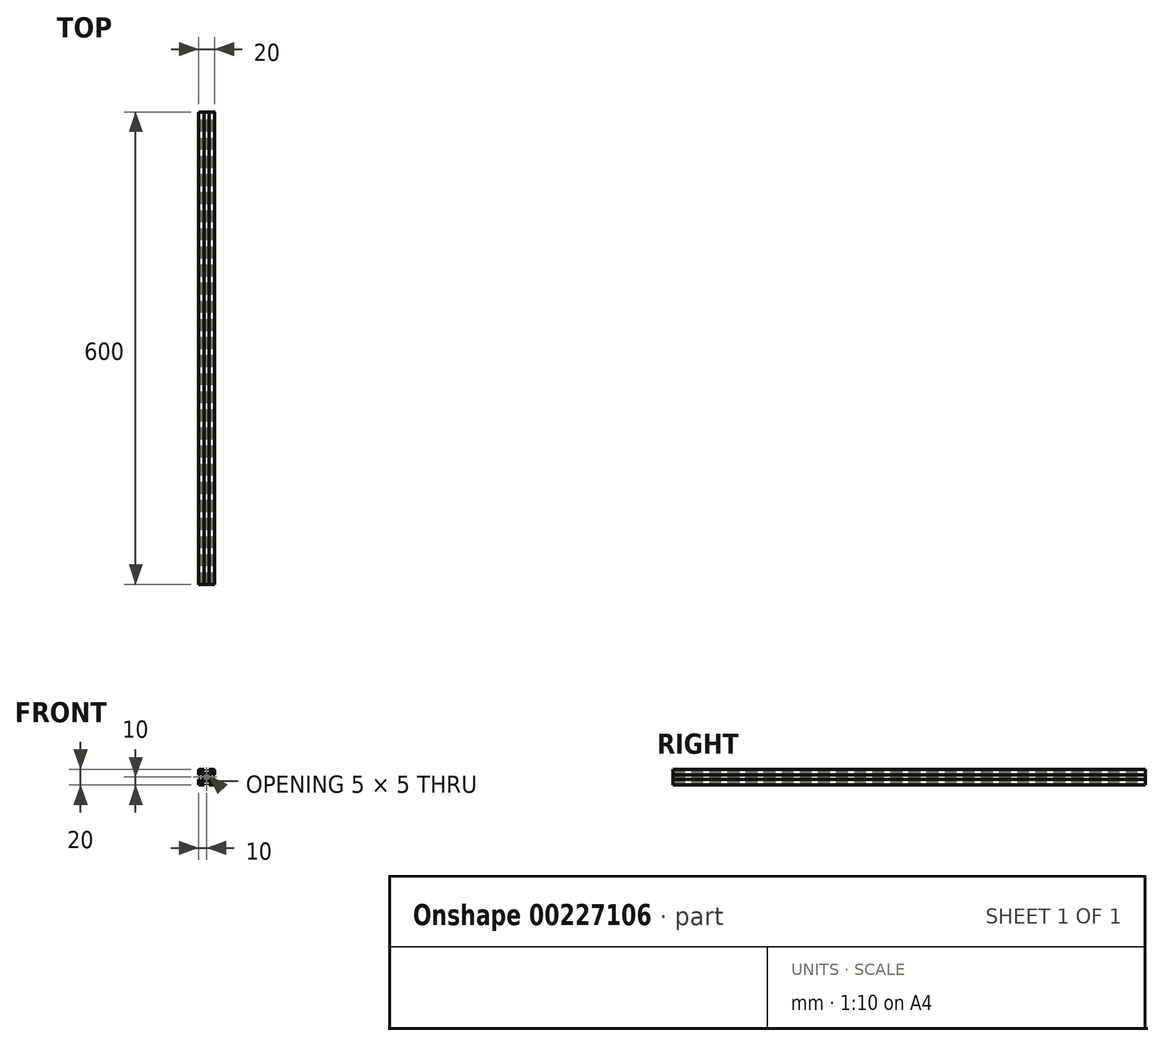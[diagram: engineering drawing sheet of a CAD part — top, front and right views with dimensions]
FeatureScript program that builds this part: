
annotation { "Feature Type Name" : "Feature", "Feature Type Description" : "" }
export const myFeature = defineFeature(function(context is Context, id is Id, definition is map)
    precondition{}
    {
        {
            var Q0;
            Q0=qCreatedBy(makeId("Front.planeOp"),FACE);
            var sketch = newSketch(context, id + "F0", { "sketchPlane" : qUnion([Q0])});
            skLineSegment(sketch, "E0.bottom", {"start": v(8.5, -10) * mm, "end": v(3, -10) * mm});
            skLineSegment(sketch, "E0.top", {"start": v(8.5, 10) * mm, "end": v(3, 10) * mm});
            skLineSegment(sketch, "E0.left", {"start": v(10, -8.5) * mm, "end": v(10, -3) * mm});
            skLineSegment(sketch, "E0.right", {"start": v(-10, -8.5) * mm, "end": v(-10, -3) * mm});
            skPoint(sketch, "E0.middle", {"position": v(0, 0) * mm});
            skLineSegment(sketch, "E1.bottom", {"start": v(6, -8.5) * mm, "end": v(3, -8.5) * mm});
            skLineSegment(sketch, "E1.top", {"start": v(6, 8.5) * mm, "end": v(3, 8.5) * mm});
            skLineSegment(sketch, "E1.left", {"start": v(8.5, -6) * mm, "end": v(8.5, -3) * mm});
            skLineSegment(sketch, "E1.right", {"start": v(-8.5, -6) * mm, "end": v(-8.5, -3) * mm});
            skLineSegment(sketch, "E2.bottom", {"start": v(3.44, -4.5) * mm, "end": v(-3.44, -4.5) * mm});
            skLineSegment(sketch, "E2.top", {"start": v(3.44, 4.5) * mm, "end": v(-3.44, 4.5) * mm});
            skLineSegment(sketch, "E2.left", {"start": v(4.5, -3.44) * mm, "end": v(4.5, 3.44) * mm});
            skLineSegment(sketch, "E2.right", {"start": v(-4.5, -3.44) * mm, "end": v(-4.5, 3.44) * mm});
            skLineSegment(sketch, "E3.bottom", {"start": v(8.5, -6) * mm, "end": v(7.06, -6) * mm});
            skLineSegment(sketch, "E3.top", {"start": v(8.5, 6) * mm, "end": v(7.06, 6) * mm});
            skLineSegment(sketch, "E4.left", {"start": v(6, -8.5) * mm, "end": v(6, -7.06) * mm});
            skLineSegment(sketch, "E4.right", {"start": v(-6, -8.5) * mm, "end": v(-6, -7.06) * mm});
            skPoint(sketch, "E5.orphan", {"position": v(-8.5, 8.5) * mm});
            skPoint(sketch, "E6.orphan", {"position": v(8.5, 8.5) * mm});
            skPoint(sketch, "E7.orphan", {"position": v(8.5, -8.5) * mm});
            skPoint(sketch, "E8.orphan", {"position": v(-8.5, -8.5) * mm});
            skLineSegment(sketch, "E9.trimOffspring", {"start": v(-6, 7.06) * mm, "end": v(-6, 8.5) * mm});
            skLineSegment(sketch, "E10.trimOffspring", {"start": v(-7.06, 6) * mm, "end": v(-8.5, 6) * mm});
            skLineSegment(sketch, "E11.trimOffspring", {"start": v(6, 7.06) * mm, "end": v(6, 8.5) * mm});
            skLineSegment(sketch, "E12.trimOffspring", {"start": v(-7.06, -6) * mm, "end": v(-8.5, -6) * mm});
            skLineSegment(sketch, "E13", {"start": v(-10, 10) * mm, "end": v(0, 0) * mm, "construction": true});
            skLineSegment(sketch, "E14", {"start": v(10, 10) * mm, "end": v(0, 0) * mm, "construction": true});
            skLineSegment(sketch, "E15", {"start": v(-6, 7.06) * mm, "end": v(-3.44, 4.5) * mm});
            skPoint(sketch, "E15.endSnap0", {"position": v(7.25, -6) * mm});
            skLineSegment(sketch, "E16", {"start": v(6, -7.06) * mm, "end": v(3.44, -4.5) * mm});
            skLineSegment(sketch, "E17", {"start": v(7.06, 6) * mm, "end": v(4.5, 3.44) * mm});
            skLineSegment(sketch, "E18", {"start": v(6, 7.06) * mm, "end": v(3.44, 4.5) * mm});
            skPoint(sketch, "E19.orphan", {"position": v(6, -6) * mm});
            skPoint(sketch, "E20.orphan", {"position": v(-4.5, -4.5) * mm});
            skPoint(sketch, "E21.orphan", {"position": v(-4.5, 4.5) * mm});
            skPoint(sketch, "E22.orphan", {"position": v(4.5, 4.5) * mm});
            skPoint(sketch, "E23.orphan", {"position": v(4.5, -4.5) * mm});
            skLineSegment(sketch, "E24.trimOffspring", {"start": v(4.5, -3.44) * mm, "end": v(7.06, -6) * mm});
            skLineSegment(sketch, "E25.trimOffspring", {"start": v(-3.44, -4.5) * mm, "end": v(-6, -7.06) * mm});
            skLineSegment(sketch, "E26.trimOffspring", {"start": v(-4.5, -3.44) * mm, "end": v(-7.06, -6) * mm});
            skLineSegment(sketch, "E27.trimOffspring", {"start": v(-4.5, 3.44) * mm, "end": v(-7.06, 6) * mm});
            skLineSegment(sketch, "E28.bottom", {"start": v(8.5, -3) * mm, "end": v(10, -3) * mm});
            skLineSegment(sketch, "E28.top", {"start": v(8.5, 3) * mm, "end": v(10, 3) * mm});
            skPoint(sketch, "E28.middle", {"position": v(10, 0) * mm});
            skLineSegment(sketch, "E29.left", {"start": v(3, 8.5) * mm, "end": v(3, 10) * mm});
            skLineSegment(sketch, "E29.right", {"start": v(-3, 8.5) * mm, "end": v(-3, 10) * mm});
            skPoint(sketch, "E29.middle", {"position": v(0, 10) * mm});
            skLineSegment(sketch, "E30.bottom", {"start": v(-8.5, 3) * mm, "end": v(-10, 3) * mm});
            skLineSegment(sketch, "E30.top", {"start": v(-8.5, -3) * mm, "end": v(-10, -3) * mm});
            skPoint(sketch, "E30.middle", {"position": v(-10, 0) * mm});
            skLineSegment(sketch, "E31.left", {"start": v(3, -8.5) * mm, "end": v(3, -10) * mm});
            skLineSegment(sketch, "E31.right", {"start": v(-3, -8.5) * mm, "end": v(-3, -10) * mm});
            skPoint(sketch, "E31.middle", {"position": v(0, -10) * mm});
            skPoint(sketch, "E32.orphan", {"position": v(3, 11.5) * mm});
            skPoint(sketch, "E33.orphan", {"position": v(-3, 11.5) * mm});
            skLineSegment(sketch, "E34.trimOffspring", {"start": v(-3, 10) * mm, "end": v(-8.5, 10) * mm});
            skLineSegment(sketch, "E35.trimOffspring", {"start": v(-3, 8.5) * mm, "end": v(-6, 8.5) * mm});
            skPoint(sketch, "E28.right.end.orphan", {"position": v(11.5, 3) * mm});
            skPoint(sketch, "E36.orphan", {"position": v(11.5, -3) * mm});
            skLineSegment(sketch, "E37.trimOffspring", {"start": v(10, 3) * mm, "end": v(10, 8.5) * mm});
            skLineSegment(sketch, "E38.trimOffspring", {"start": v(8.5, 3) * mm, "end": v(8.5, 6) * mm});
            skPoint(sketch, "E39.orphan", {"position": v(3, -11.5) * mm});
            skPoint(sketch, "E40.orphan", {"position": v(-3, -11.5) * mm});
            skLineSegment(sketch, "E41.trimOffspring", {"start": v(-3, -10) * mm, "end": v(-8.5, -10) * mm});
            skLineSegment(sketch, "E42.trimOffspring", {"start": v(-3, -8.5) * mm, "end": v(-6, -8.5) * mm});
            skPoint(sketch, "E30.right.end.orphan", {"position": v(-11.5, -3) * mm});
            skPoint(sketch, "E43.orphan", {"position": v(-11.5, 3) * mm});
            skLineSegment(sketch, "E44.trimOffspring", {"start": v(-10, 3) * mm, "end": v(-10, 8.5) * mm});
            skLineSegment(sketch, "E45.trimOffspring", {"start": v(-8.5, 3) * mm, "end": v(-8.5, 6) * mm});
            skLineSegment(sketch, "E46.trimOffspring", {"start": v(0, 0) * mm, "end": v(10, -10) * mm, "construction": true});
            skLineSegment(sketch, "E47.trimOffspring", {"start": v(0, 0) * mm, "end": v(-10, -10) * mm, "construction": true});
            skArc(sketch, "E48", {"start": v(1.16, 2.22) * mm, "mid": v(0, 2.5) * mm, "end": v(-1.16, 2.22) * mm});
            skLineSegment(sketch, "E49", {"start": v(-2.5, -1.44) * mm, "end": v(1.44, 2.5) * mm});
            skLineSegment(sketch, "E50", {"start": v(2.5, 1.44) * mm, "end": v(-1.44, -2.5) * mm});
            skLineSegment(sketch, "E51", {"start": v(1.44, -2.5) * mm, "end": v(-2.5, 1.44) * mm});
            skLineSegment(sketch, "E52", {"start": v(-1.44, 2.5) * mm, "end": v(2.5, -1.44) * mm});
            skLineSegment(sketch, "E53", {"start": v(2.5, 1.44) * mm, "end": v(2.5, -1.44) * mm, "construction": true});
            skLineSegment(sketch, "E54", {"start": v(1.44, -2.5) * mm, "end": v(-1.44, -2.5) * mm, "construction": true});
            skLineSegment(sketch, "E55", {"start": v(-2.5, -1.44) * mm, "end": v(-2.5, 1.44) * mm, "construction": true});
            skLineSegment(sketch, "E56", {"start": v(-1.44, 2.5) * mm, "end": v(1.44, 2.5) * mm, "construction": true});
            skLineSegment(sketch, "E57", {"start": v(-1.44, 2.5) * mm, "end": v(-2.5, 1.44) * mm});
            skLineSegment(sketch, "E58", {"start": v(1.44, 2.5) * mm, "end": v(2.5, 1.44) * mm});
            skLineSegment(sketch, "E59", {"start": v(2.5, -1.44) * mm, "end": v(1.44, -2.5) * mm});
            skLineSegment(sketch, "E60", {"start": v(-1.44, -2.5) * mm, "end": v(-2.5, -1.44) * mm});
            skArc(sketch, "E61.trimOffspring", {"start": v(-2.22, 1.16) * mm, "mid": v(-2.5, 0) * mm, "end": v(-2.22, -1.16) * mm});
            skArc(sketch, "E62.trimOffspring", {"start": v(-1.16, -2.22) * mm, "mid": v(0, -2.5) * mm, "end": v(1.16, -2.22) * mm});
            skArc(sketch, "E63.trimOffspring", {"start": v(2.22, -1.16) * mm, "mid": v(2.5, 0) * mm, "end": v(2.22, 1.16) * mm});
            skPoint(sketch, "E64.visualSharp", {"position": v(10, 10) * mm});
            skArc(sketch, "E64.filletArc", {"start": v(10, 8.5) * mm, "mid": v(9.56, 9.56) * mm, "end": v(8.5, 10) * mm});
            skPoint(sketch, "E65.visualSharp", {"position": v(10, -10) * mm});
            skArc(sketch, "E65.filletArc", {"start": v(8.5, -10) * mm, "mid": v(9.56, -9.56) * mm, "end": v(10, -8.5) * mm});
            skPoint(sketch, "E66.visualSharp", {"position": v(-10, -10) * mm});
            skArc(sketch, "E66.filletArc", {"start": v(-10, -8.5) * mm, "mid": v(-9.56, -9.56) * mm, "end": v(-8.5, -10) * mm});
            skPoint(sketch, "E67.visualSharp", {"position": v(-10, 10) * mm});
            skArc(sketch, "E67.filletArc", {"start": v(-8.5, 10) * mm, "mid": v(-9.56, 9.56) * mm, "end": v(-10, 8.5) * mm});
            skSolve(sketch);
        }
        {
            assignVariable(context, id + "F2", {"name" : "Length", "anyValue" : 600});
        }
        {
            var Q0;
            Q0=qSketchRegion(id+"F0",true);
            extrude(context, id + "F1", {"entities" : qUnion([Q0]), "depth" : (getVariable(context, 'Length')) * mm});
        }
    });
